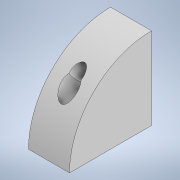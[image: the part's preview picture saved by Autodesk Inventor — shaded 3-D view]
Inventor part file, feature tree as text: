
AUTODESK INVENTOR PART (.ipt)
format: ipt  version: 2021 (Build 250183000, 183)  size: 552,960 bytes
history: native  units: mm
features: sketch x6, extrude x4, other x3, hole x2, projected_geometry x1
ambient origin geometry x8: Origin, YZ Plane, XZ Plane, XY Plane, X Axis, Y Axis, Z Axis, Center Point
bodies: Body1 (feature_tree)
feature tree (16):
  other  "實體1"
  extrude  "擠出1"  Depth=65.0mm
  hole  "孔1"  [1 undecoded]
  hole  "孔2"  [1 undecoded]
  extrude  "擠出4"  Depth=30.0mm
  extrude  "擠出5"  Depth=30.0mm
  other  "零件11"
  extrude  "擠出6"  Depth=55.0mm
  sketch  "草圖1"
  sketch  "草圖2"
  sketch  "草圖3"
  sketch  "草圖6"
  sketch  "草圖7"
  sketch  "草圖8"
  projected_geometry  "投影迴路1"
  other  "MeshFeature2"
note: 2 required parameter values undecoded (feature->parameter linkage not recoverable at this tier; creation-order binding heuristic only, values carry confidence <= 0.55)
